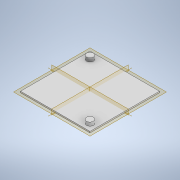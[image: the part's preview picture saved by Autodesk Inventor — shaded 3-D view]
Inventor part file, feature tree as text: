
AUTODESK INVENTOR PART (.ipt)
format: ipt  version: 2022.4 (Build 264492010, 492A)  size: 112,640 bytes
history: native  units: mm
features: extrude x2, sketch x2
ambient origin geometry x8: Origin, YZ Plane, XZ Plane, XY Plane, X Axis, Y Axis, Z Axis, Center Point
bodies: Solid1 (feature_tree)
feature tree (4):
  extrude  "Extrusion1"  Depth=50.0mm
  extrude  "Extrusion2"  Depth=2.5mm
  sketch  "Sketch1"  dims[d0=50.0mm d1=50.0mm]
  sketch  "Sketch2"  dims[d2=1.0mm d3=0.0mm d4=5.0mm d5=5.0mm d6=5.0mm d7=20.0mm d9=360.0deg d11=2.5mm d12=0.0mm]
